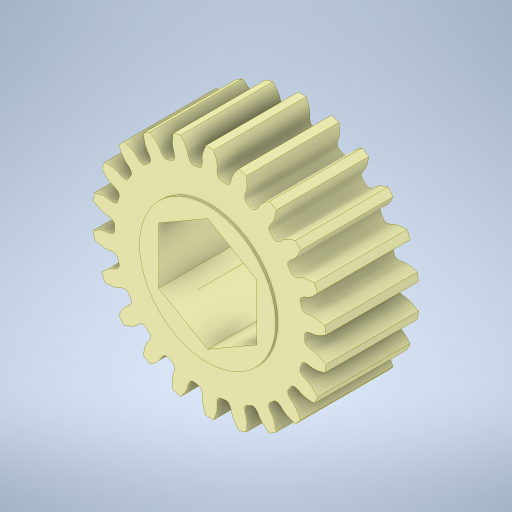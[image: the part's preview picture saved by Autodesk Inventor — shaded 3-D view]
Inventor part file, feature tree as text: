
AUTODESK INVENTOR PART (.ipt)
format: ipt  version: 2023.3 (Build 273359000, 359)  size: 516,096 bytes
history: native  units: in
note: dims shown in document units (in); Inventor stores cm internally (conversion verified against a paired STEP export)
features: other x2, plane x1
ambient origin geometry x8: Origin, YZ Plane, XZ Plane, XY Plane, X Axis, Y Axis, Z Axis, Center Point
bodies: Solid1 (feature_tree)
feature tree (3):
  plane  "Work Plane1"
  other  "Work Axis1"
  other  "Cut-Extrude1"
